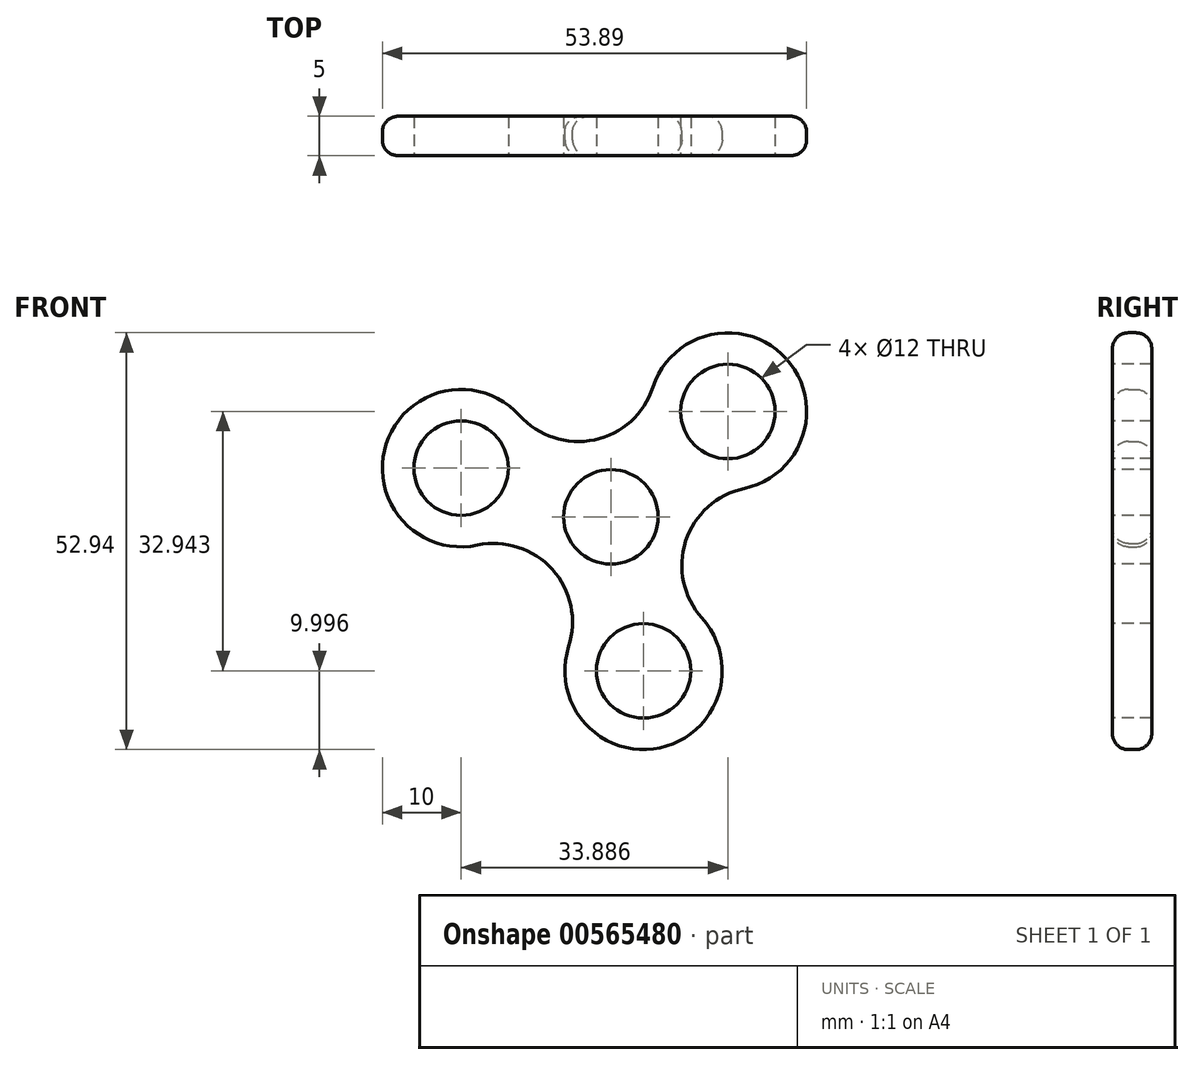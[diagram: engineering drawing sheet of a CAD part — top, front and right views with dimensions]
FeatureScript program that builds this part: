
annotation { "Feature Type Name" : "Feature", "Feature Type Description" : "" }
export const myFeature = defineFeature(function(context is Context, id is Id, definition is map)
    precondition{}
    {
        {
            var Q0;
            Q0=qCreatedBy(makeId("Front.planeOp"),FACE);
            var sketch = newSketch(context, id + "F0", { "sketchPlane" : qUnion([Q0])});
            skCircle(sketch, "E0", {"center": v(0, 0) * mm, "radius": 30 * mm});
            skPoint(sketch, "E1.0.midPoint", {"position": v(-7.43, -6.69) * mm});
            skArc(sketch, "E2", {"start": v(-11.59, 12.87) * mm, "mid": v(-28.53, 9.28) * mm, "end": v(-16.94, -3.6) * mm});
            skArc(sketch, "E3", {"start": v(-5.36, -16.47) * mm, "mid": v(6.23, -29.35) * mm, "end": v(11.59, -12.87) * mm});
            skArc(sketch, "E4", {"start": v(16.94, 3.6) * mm, "mid": v(22.3, 20.07) * mm, "end": v(5.36, 16.47) * mm});
            skArc(sketch, "E5", {"start": v(-11.59, 12.87) * mm, "mid": v(-2.08, 9.78) * mm, "end": v(5.36, 16.47) * mm});
            skArc(sketch, "E6", {"start": v(-5.36, -16.47) * mm, "mid": v(-7.43, -6.69) * mm, "end": v(-16.94, -3.6) * mm});
            skArc(sketch, "E7", {"start": v(16.94, 3.6) * mm, "mid": v(9.5, -3.1) * mm, "end": v(11.59, -12.87) * mm});
            skSolve(sketch);
        }
        {
            var Q0;
            {var subQ7=sQuery(id+"F0.wireOp",EDGE,"E5");Q0=makeQuery(id+"F0.imprint","IMPRINT",FACE,{"disambiguationData":[TD([[makeQuery(id+"F0.imprint","IMPRINT",EDGE,{"derivedFrom":subQ7}),-1.0]])]});}
            extrude(context, id + "F1", {"entities" : qUnion([Q0]), "depth" : 5 * mm, "offsetDistance" : 25 * mm});
        }
        {
            var Q0;
            Q0=makeQuery(id+"F1.opExtrude","CAP_FACE",FACE,{"disambiguationData":[OSD([sQuery(id+"F0.wireOp",EDGE,"E2"),sQuery(id+"F0.wireOp",EDGE,"E3"),sQuery(id+"F0.wireOp",EDGE,"E4"),sQuery(id+"F0.wireOp",EDGE,"E5"),sQuery(id+"F0.wireOp",EDGE,"E6"),sQuery(id+"F0.wireOp",EDGE,"E7")])],"isStart":false});
            var sketch = newSketch(context, id + "F2", { "sketchPlane" : qUnion([Q0])});
            skCircle(sketch, "E8", {"center": v(0, 0) * mm, "radius": 6 * mm});
            skCircle(sketch, "E9", {"center": v(-19.02, 6.18) * mm, "radius": 6 * mm});
            skCircle(sketch, "E10", {"center": v(14.87, 13.38) * mm, "radius": 6 * mm});
            skCircle(sketch, "E11", {"center": v(4.15, -19.56) * mm, "radius": 6 * mm});
            skSolve(sketch);
        }
        {
            var Q0;
            Q0=makeQuery(id+"F2.imprint","IMPRINT",FACE,{"disambiguationData":[TD([[makeQuery(id+"F2.imprint","IMPRINT",EDGE,{"derivedFrom":sQuery(id+"F2.wireOp",EDGE,"E9")}),1.0]])]});
            var Q1;
            Q1=makeQuery(id+"F2.imprint","IMPRINT",FACE,{"disambiguationData":[TD([[makeQuery(id+"F2.imprint","IMPRINT",EDGE,{"derivedFrom":sQuery(id+"F2.wireOp",EDGE,"E8")}),1.0]])]});
            var Q2;
            Q2=makeQuery(id+"F2.imprint","IMPRINT",FACE,{"disambiguationData":[TD([[makeQuery(id+"F2.imprint","IMPRINT",EDGE,{"derivedFrom":sQuery(id+"F2.wireOp",EDGE,"E10")}),1.0]])]});
            var Q3;
            Q3=makeQuery(id+"F2.imprint","IMPRINT",FACE,{"disambiguationData":[TD([[makeQuery(id+"F2.imprint","IMPRINT",EDGE,{"derivedFrom":sQuery(id+"F2.wireOp",EDGE,"E11")}),1.0]])]});
            extrude(context, id + "F3", {"entities" : qUnion([Q0, Q1, Q2, Q3]), "operationType" : NewBodyOperationType.REMOVE, "oppositeDirection" : true, "depth" : 25 * mm, "offsetDistance" : 25 * mm});
        }
        {
            var Q0;
            Q0=makeQuery(id+"F1.opExtrude","CAP_EDGE",EDGE,{"disambiguationData":[OSD([sQuery(id+"F0.wireOp",EDGE,"E2")])],"isStart":false});
            fillet(context, id + "F4", {"entities" : qUnion([Q0]), "radius" : 2 * mm, "tangentPropagation" : true, "allowEdgeOverflow" : false});
        }
        {
            var Q0;
            Q0=makeQuery(id+"F1.opExtrude","CAP_EDGE",EDGE,{"disambiguationData":[OSD([sQuery(id+"F0.wireOp",EDGE,"E2")])],"isStart":true});
            fillet(context, id + "F5", {"entities" : qUnion([Q0]), "radius" : 2 * mm, "tangentPropagation" : true, "allowEdgeOverflow" : false});
        }
    });
